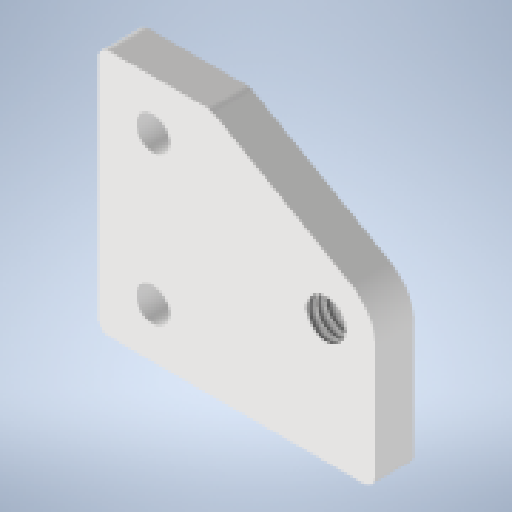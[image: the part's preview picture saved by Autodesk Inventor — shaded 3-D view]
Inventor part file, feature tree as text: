
AUTODESK INVENTOR PART (.ipt)
format: ipt  version: 2024 (Build 280153000, 153)  size: 241,152 bytes
history: native  units: mm
features: sketch x2, extrude x1, hole x1, fillet x1
ambient origin geometry x8: Origin, YZ Plane, XZ Plane, XY Plane, X Axis, Y Axis, Z Axis, Center Point
bodies: Solid1 (feature_tree)
feature tree (5):
  extrude  "Extrusion1"  Depth=40.0mm
  hole  "Hole1"  [1 undecoded]
  fillet  "Fillet1"  Radius=16.0mm
  sketch  "Sketch1"  dims[d0=40.0mm d1=9.0mm]
  sketch  "Sketch2"  dims[d2=8.0mm d3=8.0mm d4=16.0mm d5=28.0mm d6=30.0deg d7=20.0mm d8=5.4mm d9=6.35mm d10=0.0mm d11=6.4008mm d12=15.875mm d13=4.0mm d14=2.0mm d15=90.0deg d16=8.0mm d17=20.594885mm d18=2.0mm]
note: 1 required parameter value undecoded (feature->parameter linkage not recoverable at this tier; creation-order binding heuristic only, values carry confidence <= 0.55)
